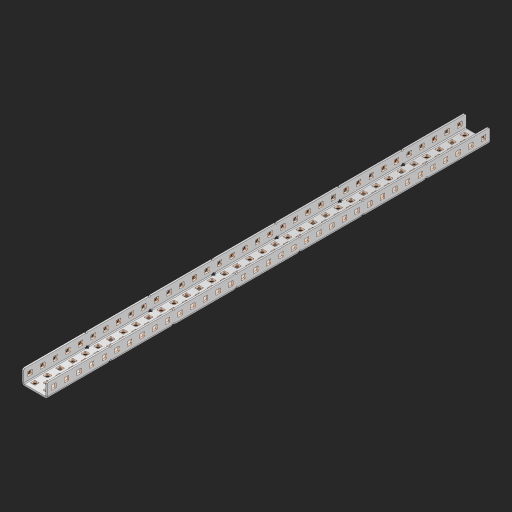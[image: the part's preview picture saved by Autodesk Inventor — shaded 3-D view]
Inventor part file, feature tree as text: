
AUTODESK INVENTOR PART (.ipt)
format: ipt  version: 2023 (Build 270158000, 158)  size: 2,057,728 bytes
history: native  units: in
note: dims shown in document units (in); Inventor stores cm internally (conversion verified against a paired STEP export)
features: other x181, extrude x172, sheet_metal_op x11, sketch x10, pattern_linear x2, mirror x1, chamfer x1
ambient origin geometry x8: Origin, YZ Plane, XZ Plane, XY Plane, X Axis, Y Axis, Z Axis, Center Point
bodies: Solid1 (feature_tree), Body (feature_tree)
feature tree (378):
  sheet_metal_op  "Flanges"
  other  "Flange Pattern Plane"
  other  "Flange Pattern Sketch"
  sheet_metal_op  "Flange Pattern"
  sheet_metal_op  "Body Pattern"
  pattern_linear  "Center Pattern"  Spacing1=0.0625in  [1 undecoded]
  other  "Arc Length"
  mirror  "Notch Mirror"
  pattern_linear  "Notch Pattern"  Spacing1=0.182in  [1 undecoded]
  chamfer  "End Chamfer"
  extrude  "Half Cut"  Depth=0.02in
  sketch  "Sketch1"  dims[d0=1.0in]
  other  "Plate1"
  sketch  "Sketch2"  dims[d1=17.5in]
  other  "Plate2"
  sheet_metal_op  "Bend1"
  sheet_metal_op  "Corner1"
  sketch  "Sketch3"  dims[d2=0.0625in]
  sketch  "Sketch7"  dims[d3=0.0625in]
  other  "Srf1"
  other  "Srf2"
  sketch  "Sketch8"  dims[d4=0.0312in]
  sketch  "Sketch9"  dims[d5=0.125in]
  other  "Srf91"
  sheet_metal_op  "Body Pattern Sketch"
  other  "Srf92"
  sketch  "Sketch13"  dims[d6=0.0625in]
  sketch  "Sketch14"  dims[d7=0.5in d8=90.0deg d9=0.0312in]
  sketch  "Sketch15"  dims[d10=0.25in]
  sketch  "Sketch16"  dims[d11=0.0625in d12=0.0625in d16=0.182in d17=0.02in d18=0.0625in d19=0.0in d20=0.25in d21=0.25in d38=13.7795in d40=0.5in d41=0.7874in d43=1.0in d46=0.172in d47=1.0in d48=0.0in d49=0.182in d50=0.02in d51=0.25in d52=0.25in d53=0.0625in d54=0.0in d55=0.172in d56=1.0in d57=0.0in d58=0.25in d60=13.7795in d62=0.5in d63=0.7874in d65=0.5in d85=0.1473in d86=0.1782in d88=0.04in d89=0.0625in d90=0.0in d91=0.04in d92=0.0491in d95=2.5in d96=0.04in d97=0.25in d98=45.0deg d99=0.25in d100=0.5in d101=0.0in d102=2.497in d106=0.182in d107=0.02in d108=0.5in d109=0.5in d110=0.0625in d111=0.0in d112=0.172in d113=0.5in d114=0.0in d117=0.5in d118=0.5in d119=0.5in]
  other  "Srf786"
  other  "Srf823"
  other  "Srf824"
  other  "Srf825"
  other  "Srf826"
  other  "Srf827"
  other  "Srf828"
  other  "Srf829"
  other  "Srf856"
  other  "Srf857"
  other  "Srf858"
  other  "Srf859"
  other  "Srf860"
  other  "Srf861"
  other  "Srf862"
  other  "Srf889"
  other  "Srf890"
  other  "Srf891"
  other  "Srf892"
  other  "Srf893"
  other  "Srf894"
  other  "Srf895"
  other  "Srf896"
  other  "Srf922"
  other  "Srf923"
  other  "Srf924"
  other  "Srf925"
  other  "Srf926"
  other  "Srf959"
  other  "Srf960"
  other  "Srf961"
  other  "Srf962"
  other  "Srf963"
  other  "Srf996"
  other  "Srf997"
  other  "Srf998"
  other  "Srf999"
  other  "Srf1000"
  other  "Srf1143"
  other  "Srf1144"
  other  "Srf1145"
  other  "Srf1146"
  other  "Srf1147"
  other  "Srf1148"
  other  "Srf1149"
  other  "Srf1150"
  other  "Srf1151"
  other  "Srf1152"
  other  "Srf1153"
  other  "Srf1154"
  other  "Srf1155"
  other  "Srf1156"
  other  "Srf1157"
  other  "Srf1158"
  other  "Srf1159"
  other  "Srf1160"
  other  "Srf1161"
  other  "Srf1162"
  other  "Srf1163"
  other  "Srf1164"
  other  "Srf1165"
  other  "Srf1166"
  other  "Srf1167"
  other  "Srf1168"
  other  "Srf1169"
  other  "Srf1170"
  other  "Srf1171"
  other  "Srf1172"
  other  "Srf1173"
  other  "Srf1174"
  other  "Srf1175"
  other  "Srf1176"
  other  "Srf1177"
  other  "Srf1178"
  other  "Srf1179"
  other  "Srf1180"
  other  "Srf1181"
  other  "Srf1182"
  other  "Srf1183"
  other  "Srf1184"
  other  "Srf1185"
  other  "Srf1186"
  other  "Srf1187"
  other  "Srf1188"
  other  "Srf1189"
  other  "Srf1190"
  other  "Srf1191"
  other  "Srf1192"
  other  "Srf1193"
  other  "Srf1194"
  other  "Srf1195"
  other  "Srf1196"
  other  "Srf1197"
  other  "Srf1198"
  other  "Srf1199"
  other  "Srf1200"
  other  "Srf1201"
  other  "Srf1202"
  other  "Srf1203"
  other  "Srf1204"
  other  "Srf1205"
  other  "Srf1206"
  other  "Srf1207"
  other  "Srf1208"
  other  "Srf1209"
  other  "Srf1210"
  other  "Srf1211"
  other  "Srf1212"
  other  "Srf1213"
  other  "Srf1214"
  other  "Srf1215"
  other  "Srf1216"
  other  "Srf1217"
  other  "Srf1218"
  other  "Srf1219"
  other  "Srf1220"
  other  "Srf1221"
  other  "Srf1222"
  other  "Srf1223"
  other  "Srf1224"
  other  "Srf1225"
  other  "Srf1226"
  other  "Srf1227"
  other  "Srf1228"
  other  "Srf1229"
  other  "Srf1230"
  other  "Srf1231"
  other  "Srf1232"
  other  "Srf1233"
  other  "Srf1234"
  other  "Srf1235"
  other  "Srf1236"
  other  "Srf1237"
  other  "Srf1238"
  other  "Srf1239"
  other  "Srf1240"
  other  "Srf1241"
  other  "Srf1242"
  other  "Srf1243"
  other  "Srf1244"
  other  "Srf1245"
  other  "Srf1246"
  other  "Srf1247"
  other  "Srf1248"
  other  "Srf1249"
  other  "Srf1250"
  other  "Srf1251"
  other  "Srf1252"
  other  "Srf1253"
  other  "Srf1254"
  other  "Srf1255"
  other  "Srf1256"
  other  "Srf1257"
  other  "Srf1258"
  other  "Srf1259"
  other  "Srf1260"
  other  "Srf1261"
  other  "Srf1262"
  other  "Srf1263"
  other  "Srf1264"
  other  "Srf1265"
  other  "Srf1266"
  other  "Srf1267"
  other  "Srf1268"
  other  "Srf1269"
  other  "Srf1270"
  other  "Srf1271"
  other  "Srf1272"
  other  "Srf1273"
  other  "Srf1274"
  sheet_metal_op  "Flange Stamp"
  sheet_metal_op  "Flange Circle"
  sheet_metal_op  "Body Stamp"
  sheet_metal_op  "Body Circle"
  other  "Center Stamp"
  other  "Center Circle"
  sheet_metal_op  "Notch"
  extrude  "ExtrusionSrf2"  Depth=0.0625in
  extrude  "ExtrusionSrf92"  TaperAngle=0.0deg  [1 undecoded]
  extrude  "ExtrusionSrf823"  Depth=0.5in
  extrude  "ExtrusionSrf824"  Depth=0.5in
  extrude  "ExtrusionSrf825"  Depth=0.5in
  extrude  "ExtrusionSrf826"  Depth=0.5in
  extrude  "ExtrusionSrf827"  Depth=1.0in TaperAngle=0.0deg
  extrude  "ExtrusionSrf828"  Depth=0.5in
  extrude  "ExtrusionSrf829"  Depth=0.02in
  extrude  "ExtrusionSrf856"  Depth=0.5in
  extrude  "ExtrusionSrf857"  Depth=0.5in
  extrude  "ExtrusionSrf858"  Depth=0.0625in
  extrude  "ExtrusionSrf859"  TaperAngle=0.0deg  [1 undecoded]
  extrude  "ExtrusionSrf860"  Depth=0.5in
  extrude  "ExtrusionSrf861"  Depth=1.0in TaperAngle=0.0deg
  extrude  "ExtrusionSrf862"  Depth=0.5in
  extrude  "ExtrusionSrf889"  Depth=0.5in
  extrude  "ExtrusionSrf890"  Depth=0.5in
  extrude  "ExtrusionSrf891"  Depth=0.5in
  extrude  "ExtrusionSrf892"  Depth=0.5in
  extrude  "ExtrusionSrf893"  Depth=0.5in
  extrude  "ExtrusionSrf894"  Depth=0.0625in
  extrude  "ExtrusionSrf895"  TaperAngle=0.0deg  [1 undecoded]
  extrude  "ExtrusionSrf896"  Depth=0.5in
  extrude  "ExtrusionSrf922"  Depth=0.5in
  extrude  "ExtrusionSrf923"  Depth=2.5in
  extrude  "ExtrusionSrf924"  Depth=0.5in TaperAngle=45.0deg
  extrude  "ExtrusionSrf925"  Depth=0.5in
  extrude  "ExtrusionSrf926"  Depth=0.5in TaperAngle=0.0deg
  extrude  "ExtrusionSrf959"  Depth=0.5in
  extrude  "ExtrusionSrf960"  Depth=0.5in
  extrude  "ExtrusionSrf961"  Depth=0.02in
  extrude  "ExtrusionSrf962"  Depth=0.5in
  extrude  "ExtrusionSrf963"  Depth=0.5in
  extrude  "ExtrusionSrf996"  Depth=0.0625in
  extrude  "ExtrusionSrf997"  TaperAngle=0.0deg  [1 undecoded]
  extrude  "ExtrusionSrf998"  Depth=0.5in
  extrude  "ExtrusionSrf999"  Depth=0.5in TaperAngle=0.0deg
  extrude  "ExtrusionSrf1000"  Depth=0.5in
  extrude  "ExtrusionSrf1143"  Depth=0.5in
  extrude  "ExtrusionSrf1144"  Depth=0.5in
  extrude  "ExtrusionSrf1145"  [1 undecoded]
  extrude  "ExtrusionSrf1146"  [1 undecoded]
  extrude  "ExtrusionSrf1147"  [1 undecoded]
  extrude  "ExtrusionSrf1148"  [1 undecoded]
  extrude  "ExtrusionSrf1149"  [1 undecoded]
  extrude  "ExtrusionSrf1150"  [1 undecoded]
  extrude  "ExtrusionSrf1151"  [1 undecoded]
  extrude  "ExtrusionSrf1152"  [1 undecoded]
  extrude  "ExtrusionSrf1153"  [1 undecoded]
  extrude  "ExtrusionSrf1154"  [1 undecoded]
  extrude  "ExtrusionSrf1155"  [1 undecoded]
  extrude  "ExtrusionSrf1156"  [1 undecoded]
  extrude  "ExtrusionSrf1157"  [1 undecoded]
  extrude  "ExtrusionSrf1158"  [1 undecoded]
  extrude  "ExtrusionSrf1159"  [1 undecoded]
  extrude  "ExtrusionSrf1160"  [1 undecoded]
  extrude  "ExtrusionSrf1161"  [1 undecoded]
  extrude  "ExtrusionSrf1162"  [1 undecoded]
  extrude  "ExtrusionSrf1163"  [1 undecoded]
  extrude  "ExtrusionSrf1164"  [1 undecoded]
  extrude  "ExtrusionSrf1165"  [1 undecoded]
  extrude  "ExtrusionSrf1166"  [1 undecoded]
  extrude  "ExtrusionSrf1167"  [1 undecoded]
  extrude  "ExtrusionSrf1168"  [1 undecoded]
  extrude  "ExtrusionSrf1169"  [1 undecoded]
  extrude  "ExtrusionSrf1170"  [1 undecoded]
  extrude  "ExtrusionSrf1171"  [1 undecoded]
  extrude  "ExtrusionSrf1172"  [1 undecoded]
  extrude  "ExtrusionSrf1173"  [1 undecoded]
  extrude  "ExtrusionSrf1174"  [1 undecoded]
  extrude  "ExtrusionSrf1175"  [1 undecoded]
  extrude  "ExtrusionSrf1176"  [1 undecoded]
  extrude  "ExtrusionSrf1177"  [1 undecoded]
  extrude  "ExtrusionSrf1178"  [1 undecoded]
  extrude  "ExtrusionSrf1179"  [1 undecoded]
  extrude  "ExtrusionSrf1180"  [1 undecoded]
  extrude  "ExtrusionSrf1181"  [1 undecoded]
  extrude  "ExtrusionSrf1182"  [1 undecoded]
  extrude  "ExtrusionSrf1183"  [1 undecoded]
  extrude  "ExtrusionSrf1184"  [1 undecoded]
  extrude  "ExtrusionSrf1185"  [1 undecoded]
  extrude  "ExtrusionSrf1186"  [1 undecoded]
  extrude  "ExtrusionSrf1187"  [1 undecoded]
  extrude  "ExtrusionSrf1188"  [1 undecoded]
  extrude  "ExtrusionSrf1189"  [1 undecoded]
  extrude  "ExtrusionSrf1190"  [1 undecoded]
  extrude  "ExtrusionSrf1191"  [1 undecoded]
  extrude  "ExtrusionSrf1192"  [1 undecoded]
  extrude  "ExtrusionSrf1193"  [1 undecoded]
  extrude  "ExtrusionSrf1194"  [1 undecoded]
  extrude  "ExtrusionSrf1195"  [1 undecoded]
  extrude  "ExtrusionSrf1196"  [1 undecoded]
  extrude  "ExtrusionSrf1197"  [1 undecoded]
  extrude  "ExtrusionSrf1198"  [1 undecoded]
  extrude  "ExtrusionSrf1199"  [1 undecoded]
  extrude  "ExtrusionSrf1200"  [1 undecoded]
  extrude  "ExtrusionSrf1201"  [1 undecoded]
  extrude  "ExtrusionSrf1202"  [1 undecoded]
  extrude  "ExtrusionSrf1203"  [1 undecoded]
  extrude  "ExtrusionSrf1204"  [1 undecoded]
  extrude  "ExtrusionSrf1205"  [1 undecoded]
  extrude  "ExtrusionSrf1206"  [1 undecoded]
  extrude  "ExtrusionSrf1207"  [1 undecoded]
  extrude  "ExtrusionSrf1208"  [1 undecoded]
  extrude  "ExtrusionSrf1209"  [1 undecoded]
  extrude  "ExtrusionSrf1210"  [1 undecoded]
  extrude  "ExtrusionSrf1211"  [1 undecoded]
  extrude  "ExtrusionSrf1212"  [1 undecoded]
  extrude  "ExtrusionSrf1213"  [1 undecoded]
  extrude  "ExtrusionSrf1214"  [1 undecoded]
  extrude  "ExtrusionSrf1215"  [1 undecoded]
  extrude  "ExtrusionSrf1216"  [1 undecoded]
  extrude  "ExtrusionSrf1217"  [1 undecoded]
  extrude  "ExtrusionSrf1218"  [1 undecoded]
  extrude  "ExtrusionSrf1219"  [1 undecoded]
  extrude  "ExtrusionSrf1220"  [1 undecoded]
  extrude  "ExtrusionSrf1221"  [1 undecoded]
  extrude  "ExtrusionSrf1222"  [1 undecoded]
  extrude  "ExtrusionSrf1223"  [1 undecoded]
  extrude  "ExtrusionSrf1224"  [1 undecoded]
  extrude  "ExtrusionSrf1225"  [1 undecoded]
  extrude  "ExtrusionSrf1226"  [1 undecoded]
  extrude  "ExtrusionSrf1227"  [1 undecoded]
  extrude  "ExtrusionSrf1228"  [1 undecoded]
  extrude  "ExtrusionSrf1229"  [1 undecoded]
  extrude  "ExtrusionSrf1230"  [1 undecoded]
  extrude  "ExtrusionSrf1231"  [1 undecoded]
  extrude  "ExtrusionSrf1232"  [1 undecoded]
  extrude  "ExtrusionSrf1233"  [1 undecoded]
  extrude  "ExtrusionSrf1234"  [1 undecoded]
  extrude  "ExtrusionSrf1235"  [1 undecoded]
  extrude  "ExtrusionSrf1236"  [1 undecoded]
  extrude  "ExtrusionSrf1237"  [1 undecoded]
  extrude  "ExtrusionSrf1238"  [1 undecoded]
  extrude  "ExtrusionSrf1239"  [1 undecoded]
  extrude  "ExtrusionSrf1240"  [1 undecoded]
  extrude  "ExtrusionSrf1241"  [1 undecoded]
  extrude  "ExtrusionSrf1242"  [1 undecoded]
  extrude  "ExtrusionSrf1243"  [1 undecoded]
  extrude  "ExtrusionSrf1244"  [1 undecoded]
  extrude  "ExtrusionSrf1245"  [1 undecoded]
  extrude  "ExtrusionSrf1246"  [1 undecoded]
  extrude  "ExtrusionSrf1247"  [1 undecoded]
  extrude  "ExtrusionSrf1248"  [1 undecoded]
  extrude  "ExtrusionSrf1249"  [1 undecoded]
  extrude  "ExtrusionSrf1250"  [1 undecoded]
  extrude  "ExtrusionSrf1251"  [1 undecoded]
  extrude  "ExtrusionSrf1252"  [1 undecoded]
  extrude  "ExtrusionSrf1253"  [1 undecoded]
  extrude  "ExtrusionSrf1254"  [1 undecoded]
  extrude  "ExtrusionSrf1255"  [1 undecoded]
  extrude  "ExtrusionSrf1256"  [1 undecoded]
  extrude  "ExtrusionSrf1257"  [1 undecoded]
  extrude  "ExtrusionSrf1258"  [1 undecoded]
  extrude  "ExtrusionSrf1259"  [1 undecoded]
  extrude  "ExtrusionSrf1260"  [1 undecoded]
  extrude  "ExtrusionSrf1261"  [1 undecoded]
  extrude  "ExtrusionSrf1262"  [1 undecoded]
  extrude  "ExtrusionSrf1263"  [1 undecoded]
  extrude  "ExtrusionSrf1264"  [1 undecoded]
  extrude  "ExtrusionSrf1265"  [1 undecoded]
  extrude  "ExtrusionSrf1266"  [1 undecoded]
  extrude  "ExtrusionSrf1267"  [1 undecoded]
  extrude  "ExtrusionSrf1268"  [1 undecoded]
  extrude  "ExtrusionSrf1269"  [1 undecoded]
  extrude  "ExtrusionSrf1270"  [1 undecoded]
  extrude  "ExtrusionSrf1271"  [1 undecoded]
  extrude  "ExtrusionSrf1272"  [1 undecoded]
  extrude  "ExtrusionSrf1273"  [1 undecoded]
  extrude  "ExtrusionSrf1274"  [1 undecoded]
note: 136 required parameter values undecoded (feature->parameter linkage not recoverable at this tier; creation-order binding heuristic only, values carry confidence <= 0.55)
